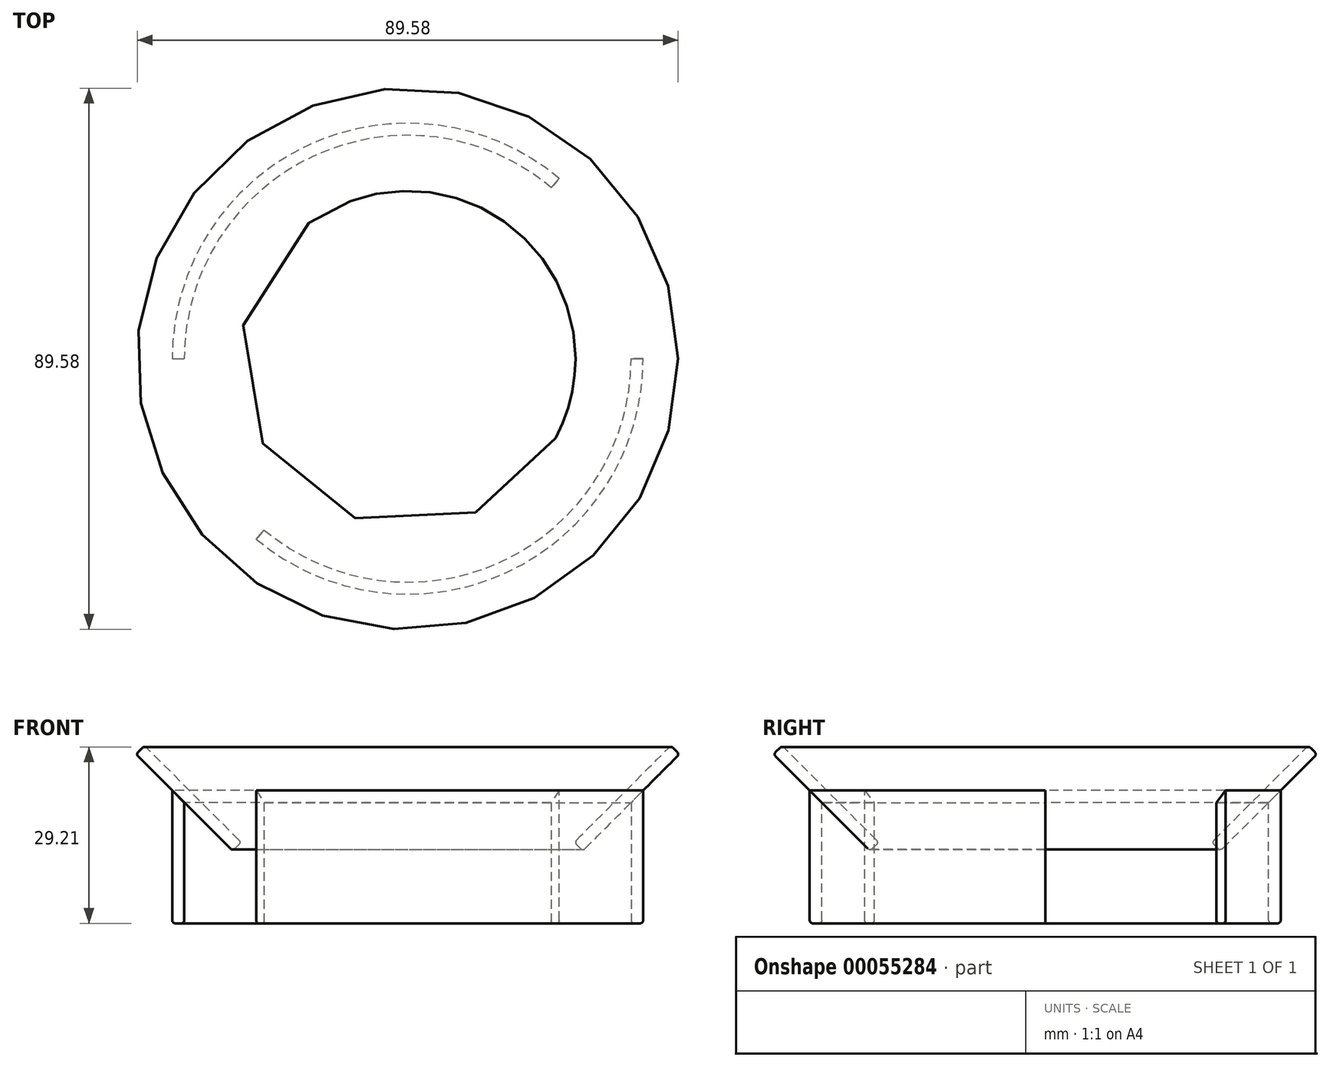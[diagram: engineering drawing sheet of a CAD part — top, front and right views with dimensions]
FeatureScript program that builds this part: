
annotation { "Feature Type Name" : "Feature", "Feature Type Description" : "" }
export const myFeature = defineFeature(function(context is Context, id is Id, definition is map)
    precondition{}
    {
        {
            var Q0;
            Q0=qCreatedBy(makeId("Front.planeOp"),FACE);
            var sketch = newSketch(context, id + "F0", { "sketchPlane" : qUnion([Q0])});
            skLineSegment(sketch, "E0", {"start": v(-39, 2) * mm, "end": v(-39, -19) * mm});
            skLineSegment(sketch, "E1", {"start": v(-37, 0) * mm, "end": v(-37, -19) * mm});
            skLineSegment(sketch, "E2", {"start": v(39, 2) * mm, "end": v(39, -19) * mm});
            skLineSegment(sketch, "E3", {"start": v(37, -19) * mm, "end": v(37, 0) * mm});
            skLineSegment(sketch, "E4", {"start": v(-38.5, -19.5) * mm, "end": v(-37.5, -19.5) * mm});
            skLineSegment(sketch, "E5", {"start": v(-39, 2) * mm, "end": v(-39, 2.5) * mm});
            skLineSegment(sketch, "E6", {"start": v(-39, 2.5) * mm, "end": v(-37, 0.5) * mm});
            skLineSegment(sketch, "E7", {"start": v(-37, 0.5) * mm, "end": v(-37, 0) * mm});
            skLineSegment(sketch, "E8", {"start": v(39, 2) * mm, "end": v(39, 2.5) * mm});
            skLineSegment(sketch, "E9", {"start": v(39, 2.5) * mm, "end": v(37, 0.5) * mm});
            skLineSegment(sketch, "E10", {"start": v(37, 0.5) * mm, "end": v(37, 0) * mm});
            skPoint(sketch, "E11.visualSharp", {"position": v(-39, -19.5) * mm});
            skArc(sketch, "E11.filletArc", {"start": v(-39, -19) * mm, "mid": v(-38.85, -19.35) * mm, "end": v(-38.5, -19.5) * mm});
            skPoint(sketch, "E12.visualSharp", {"position": v(-37, -19.5) * mm});
            skArc(sketch, "E12.filletArc", {"start": v(-37.5, -19.5) * mm, "mid": v(-37.15, -19.35) * mm, "end": v(-37, -19) * mm});
            skLineSegment(sketch, "E13", {"start": v(37.5, -19.5) * mm, "end": v(38.5, -19.5) * mm});
            skPoint(sketch, "E14.visualSharp", {"position": v(37, -19.5) * mm});
            skArc(sketch, "E14.filletArc", {"start": v(37, -19) * mm, "mid": v(37.15, -19.35) * mm, "end": v(37.5, -19.5) * mm});
            skPoint(sketch, "E15.visualSharp", {"position": v(39, -19.5) * mm});
            skArc(sketch, "E15.filletArc", {"start": v(38.5, -19.5) * mm, "mid": v(38.85, -19.35) * mm, "end": v(39, -19) * mm});
            skSolve(sketch);
        }
        {
            var Q0;
            Q0=qCreatedBy(makeId("Front.planeOp"),FACE);
            var sketch = newSketch(context, id + "F1", { "sketchPlane" : qUnion([Q0])});
            skLineSegment(sketch, "E16", {"start": v(0, 39.76) * mm, "end": v(0, -60.38) * mm});
            skSolve(sketch);
        }
        {
            var Q0;
            Q0=qCreatedBy(makeId("Front.planeOp"),FACE);
            var sketch = newSketch(context, id + "F2", { "sketchPlane" : qUnion([Q0])});
            skLineSegment(sketch, "E17", {"start": v(-28.65, -7.15) * mm, "end": v(-27.94, -6.44) * mm});
            skLineSegment(sketch, "E18", {"start": v(-27.94, -5.73) * mm, "end": v(-43.23, 9.56) * mm});
            skLineSegment(sketch, "E19", {"start": v(-44.65, 8.85) * mm, "end": v(-43.94, 9.56) * mm});
            skLineSegment(sketch, "E20", {"start": v(-44.65, 8.15) * mm, "end": v(-29.35, -7.15) * mm});
            skPoint(sketch, "E21.visualSharp", {"position": v(-45, 8.5) * mm});
            skArc(sketch, "E21.filletArc", {"start": v(-44.65, 8.85) * mm, "mid": v(-44.8, 8.5) * mm, "end": v(-44.65, 8.15) * mm});
            skPoint(sketch, "E22.visualSharp", {"position": v(-43.59, 9.91) * mm});
            skArc(sketch, "E22.filletArc", {"start": v(-43.23, 9.56) * mm, "mid": v(-43.59, 9.7) * mm, "end": v(-43.94, 9.56) * mm});
            skPoint(sketch, "E23.visualSharp", {"position": v(-27.59, -6.09) * mm});
            skArc(sketch, "E23.filletArc", {"start": v(-27.94, -6.44) * mm, "mid": v(-27.8, -6.09) * mm, "end": v(-27.94, -5.73) * mm});
            skPoint(sketch, "E24.visualSharp", {"position": v(-29, -7.5) * mm});
            skArc(sketch, "E24.filletArc", {"start": v(-29.35, -7.15) * mm, "mid": v(-29, -7.3) * mm, "end": v(-28.65, -7.15) * mm});
            skSolve(sketch);
        }
        {
            var Q0;
            Q0 = qSketchRegion(id + "F0", true);
            var Q1;
            Q1=sQuery(id+"F1.wireOp",EDGE,"E16");
            revolve(context, id + "F3", {"entities" : qUnion([Q0]), "axis" : qUnion([Q1]), "revolveType" : RevolveType.ONE_DIRECTION, "angle" : 130 * degree});
        }
        {
            var Q0;
            Q0=qCreatedBy(makeId("Front.planeOp"),FACE);
            var sketch = newSketch(context, id + "F4", { "sketchPlane" : qUnion([Q0])});
            skLineSegment(sketch, "E25", {"start": v(0, 19.24) * mm, "end": v(0, -42.33) * mm});
            skSolve(sketch);
        }
        {
            var Q0;
            Q0 = qSketchRegion(id + "F2", true);
            var Q1;
            Q1=sQuery(id+"F4.wireOp",EDGE,"E25");
            revolve(context, id + "F5", {"entities" : qUnion([Q0]), "axis" : qUnion([Q1]), "revolveType" : RevolveType.FULL});
        }
    });
